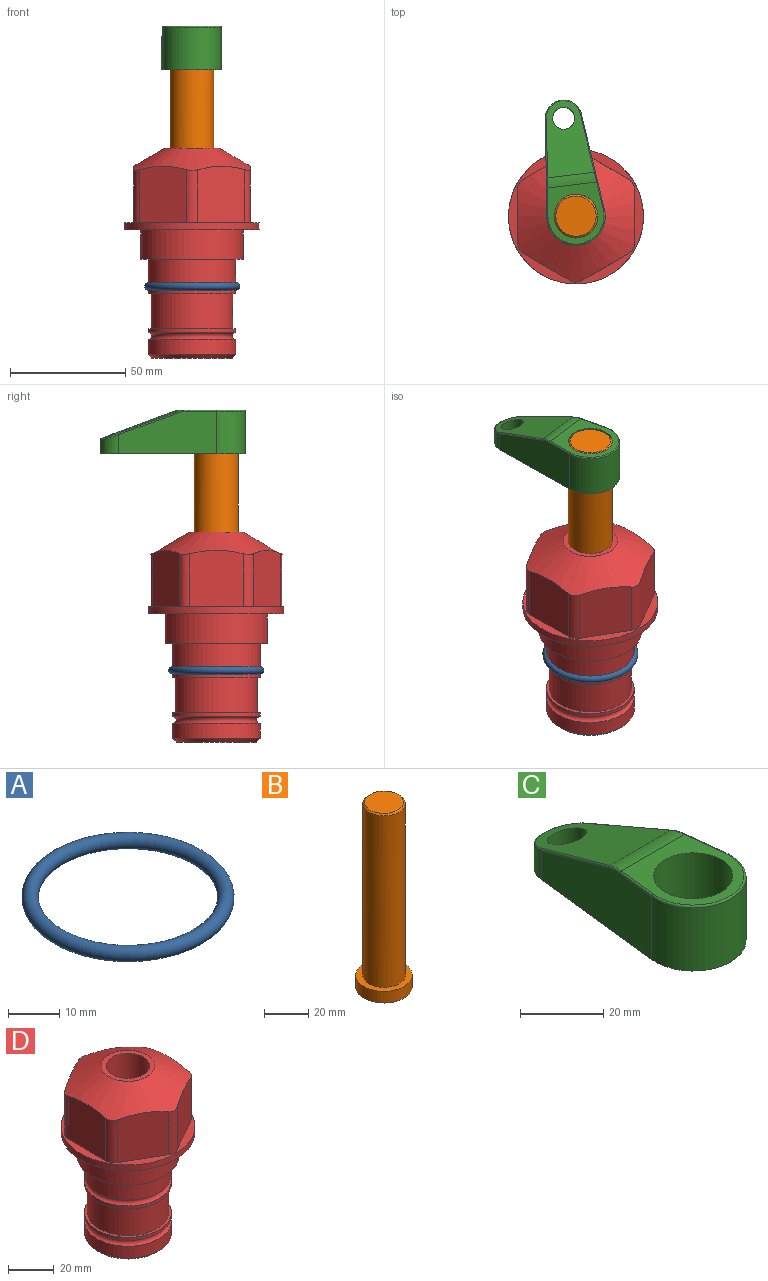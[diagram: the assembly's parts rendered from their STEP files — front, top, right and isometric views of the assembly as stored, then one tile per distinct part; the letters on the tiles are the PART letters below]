
ASSEMBLY  parts=4 mates=2
PART A: 1 faces, bbox 44.7x44.7x3.2 mm
  f0: torus R=19.05mm, axis (0,0,1), area 1193.9mm2
PART B: 6 faces, bbox 25.4x25.4x101.6 mm
  f0: plane 17.46x17.46mm, normal (0,0,1), area 239.5mm2, adj f5
  f1: plane 25.4x25.4mm, normal (0,0,-1), area 506.7mm2, adj f2
  f2: cylinder r=12.7mm len=25.4mm, axis (0,0,1), area 506.7mm2, adj f1,f3
  f3: plane 25.4x25.4mm, normal (0,0,1), area 221.7mm2, adj f2,f4
  f4: cylinder r=9.53mm len=94.46mm, axis (0,0,1), area 5653mm2, adj f3,f5
  f5: cone r=8.73mm half-angle=45deg, axis (0,0,-1), area 64.4mm2, adj f0,f4
PART C: 44 faces, bbox 27.5x64.5x19.1 mm
  f0: plane 2.3x0.95mm, normal (0,0,-1), area 1mm2, adj f25,f30,f34
  f1: plane 63.5x25.4mm, normal (0,0,-1), area 561.7mm2, adj f2,f3,f4,f5,f6,f7,f19,f20
  f2: cylinder r=12.7mm len=25.4mm, axis (0,0,-1), area 792.2mm2, adj f1,f3,f5,f13
  f3: plane 42.33x18.54mm, normal (0.99,0.11,0), area 647mm2, adj f1,f2,f4,f11,f12,f14
  f4: cylinder r=7.94mm len=15.78mm, axis (0,0,-1), area 158.6mm2, adj f1,f3,f5,f16
  f5: plane 42.33x18.54mm, normal (-0.99,0.11,0), area 647mm2, adj f1,f2,f4,f15,f17,f18
  f6: cylinder r=9.53mm len=19.05mm, axis (0,0,-1), area 1140.1mm2, adj f1,f8
  f7: cylinder r=4.76mm len=10.98mm, axis (0,0,-1), area 276.1mm2, adj f1,f9
  f8: plane 25.83x24.38mm, normal (0,0,1), area 262.2mm2, adj f6,f10,f11,f13,f15
  f9: plane 32.49x20.55mm, normal (0,0.34,0.94), area 489.9mm2, adj f7,f10,f14,f16,f18
  f10: cylinder r=12.7mm len=21.49mm, axis (-1,0,0), area 93.2mm2, adj f8,f9,f12,f17
  f11: cylinder r=0.51mm len=12.34mm, axis (0.11,-0.99,0), area 9.9mm2, adj f3,f8,f12,f13
  f12: bspline ~7.62x1.64mm, area 3.5mm2, adj f3,f10,f11,f14
  f13: torus R=12.19mm, axis (0,0,1), area 33.6mm2, adj f2,f8,f11,f15
  f14: cylinder r=0.51mm len=26.01mm, axis (0.1,-0.93,0.34), area 21.6mm2, adj f3,f9,f12,f16
  f15: cylinder r=0.51mm len=12.34mm, axis (0.11,0.99,0), area 9.9mm2, adj f5,f8,f13,f17
  f16: bspline ~15.78x7.05mm, area 15.7mm2, adj f4,f9,f14,f18
  f17: bspline ~7.62x1.64mm, area 3.5mm2, adj f5,f10,f15,f18
  f18: cylinder r=0.51mm len=26.01mm, axis (0.1,0.93,-0.34), area 21.6mm2, adj f5,f9,f16,f17
  f19: plane 21.6x14.29mm, normal (-0.99,-0.11,0), area 242.6mm2, adj f1,f26,f28,f34,f36,f38
  f20: plane 21.6x14.29mm, normal (0.99,-0.11,0), area 242.6mm2, adj f1,f27,f29,f37,f39,f41
  f21: cylinder r=12.7mm len=14.29mm, axis (0,0,-1), area 173.2mm2, adj f1,f26,f27,f30,f31,f33
  f22: cylinder r=7.94mm len=7.63mm, axis (0,0,-1), area 53.8mm2, adj f1,f28,f29,f42
  f23: plane 2.3x0.95mm, normal (0,0,-1), area 1mm2, adj f25,f33,f37
  f24: plane 17.94x12.32mm, normal (0,-0.34,-0.94), area 191.2mm2, adj f25,f38,f41,f42
  f25: cylinder r=9.53mm len=12.93mm, axis (-1,0,0), area 37.5mm2, adj f0,f23,f24,f31,f36,f39
  f26: cylinder r=1.59mm len=14.29mm, axis (0,0,-1), area 49mm2, adj f1,f19,f21,f32
  f27: cylinder r=1.59mm len=14.29mm, axis (0,0,-1), area 49mm2, adj f1,f20,f21,f35
  f28: cylinder r=1.59mm len=7.28mm, axis (0,0,-1), area 22.1mm2, adj f1,f19,f22,f40
  f29: cylinder r=1.59mm len=7.28mm, axis (0,0,-1), area 22.1mm2, adj f1,f20,f22,f43
  f30: torus R=14.29mm, axis (0,0,1), area 5.8mm2, adj f0,f21,f31,f32
  f31: bspline ~11.06x2.73mm, area 20.8mm2, adj f21,f25,f30,f33
  f32: sphere r=1.59mm, area 5.4mm2, adj f26,f30,f34
  f33: torus R=14.29mm, axis (0,0,1), area 5.8mm2, adj f21,f23,f31,f35
  f34: cylinder r=1.59mm len=1.68mm, axis (-0.11,0.99,0), area 2.4mm2, adj f0,f19,f32,f36
  f35: sphere r=1.59mm, area 5.4mm2, adj f27,f33,f37
  f36: bspline ~5.82x2.33mm, area 7.7mm2, adj f19,f25,f34,f38
  f37: cylinder r=1.59mm len=1.68mm, axis (0.11,0.99,0), area 2.4mm2, adj f20,f23,f35,f39
  f38: cylinder r=1.59mm len=18.33mm, axis (0.1,-0.93,0.34), area 46.7mm2, adj f19,f24,f36,f40
  f39: bspline ~5.82x2.33mm, area 7.7mm2, adj f20,f25,f37,f41
  f40: sphere r=1.59mm, area 3.6mm2, adj f28,f38,f42
  f41: cylinder r=1.59mm len=18.33mm, axis (0.1,0.93,-0.34), area 46.7mm2, adj f20,f24,f39,f43
  f42: bspline ~8.31x1.84mm, area 15.3mm2, adj f22,f24,f40,f43
  f43: sphere r=1.59mm, area 3.6mm2, adj f29,f41,f42
PART D: 36 faces, bbox 58.7x58.7x91.2 mm
  f0: cylinder r=17.78mm len=35.56mm, axis (0,0,1), area 1670.8mm2, adj f23,f24,f31
  f1: cylinder r=19.05mm len=38.1mm, axis (0,0,1), area 1191.9mm2, adj f26,f27,f30
  f2: plane 58.66x58.66mm, normal (0,0,-1), area 1150.6mm2, adj f3,f28
  f3: cylinder r=29.33mm len=58.66mm, axis (0,0,-1), area 585.1mm2, adj f2,f4
  f4: plane 58.66x58.66mm, normal (0,0,1), area 475.9mm2, adj f3,f5,f6,f7,f8,f9,f10,f11
  f5: plane 24.5x20.32mm, normal (-0.5,0.87,0), area 562.8mm2, adj f4,f15,f16,f17
  f6: plane 24.5x20.32mm, normal (0.5,0.87,0), area 562.8mm2, adj f4,f14,f15,f17
  f7: plane 24.5x23.48mm, normal (1,0,0), area 562.8mm2, adj f4,f13,f14,f17
  f8: plane 24.5x20.32mm, normal (0.5,-0.87,0), area 562.8mm2, adj f4,f12,f13,f17
  f9: plane 24.5x20.32mm, normal (-0.5,-0.87,0), area 562.8mm2, adj f4,f11,f12,f17
  f10: plane 24.5x23.48mm, normal (-1,0,0), area 562.8mm2, adj f4,f11,f16,f17
  f11: cylinder r=5.08mm len=23.01mm, axis (0,0,-1), area 121.2mm2, adj f4,f9,f10,f17
  f12: cylinder r=5.08mm len=23.01mm, axis (0,0,-1), area 121.2mm2, adj f4,f8,f9,f17
  f13: cylinder r=5.08mm len=23.01mm, axis (0,0,-1), area 121.2mm2, adj f4,f7,f8,f17
  f14: cylinder r=5.08mm len=23.01mm, axis (0,0,-1), area 121.2mm2, adj f4,f6,f7,f17
  f15: cylinder r=5.08mm len=23.01mm, axis (0,0,-1), area 121.2mm2, adj f4,f5,f6,f17
  f16: cylinder r=5.08mm len=23.01mm, axis (0,0,-1), area 121.2mm2, adj f4,f5,f10,f17
  f17: cone r=11.73mm half-angle=60deg, axis (0,0,-1), area 2071.8mm2, adj f5,f6,f7,f8,f9,f10,f11,f12
  f18: plane 23.46x23.46mm, normal (0,0,1), area 147.4mm2, adj f17,f35
  f19: plane 34.93x34.93mm, normal (0,0,-1), area 958mm2, adj f29
  f20: cylinder r=19.05mm len=38.1mm, axis (0,0,1), area 760.1mm2, adj f21,f29
  f21: torus R=19.05mm, axis (0,0,1), area 565.3mm2, adj f20,f22
  f22: cylinder r=19.05mm len=38.1mm, axis (0,0,1), area 190mm2, adj f21,f23
  f23: plane 38.1x38.1mm, normal (0,0,1), area 146.9mm2, adj f0,f22
  f24: plane 38.1x38.1mm, normal (0,0,-1), area 146.9mm2, adj f0,f25
  f25: cylinder r=19.05mm len=38.1mm, axis (0,0,1), area 190mm2, adj f24,f26
  f26: torus R=19.05mm, axis (0,0,1), area 565.3mm2, adj f1,f25
  f27: plane 44.45x44.45mm, normal (0,0,-1), area 411.7mm2, adj f1,f28
  f28: cylinder r=22.23mm len=44.45mm, axis (0,0,1), area 1773.5mm2, adj f2,f27
  f29: cone r=19.05mm half-angle=45deg, axis (0,0,1), area 257.5mm2, adj f19,f20
  f30: cylinder r=3.17mm len=6.75mm, axis (-1,0,0), area 128mm2, adj f1,f33
  f31: cylinder r=3.17mm len=6.35mm, axis (-1,0,0), area 102.5mm2, adj f0,f33
  f32: plane 25.4x25.4mm, normal (0,0,1), area 506.7mm2, adj f33
  f33: cylinder r=12.7mm len=66.42mm, axis (0,0,-1), area 5236.2mm2, adj f30,f31,f32,f34
  f34: cone r=9.53mm half-angle=30deg, axis (0,0,-1), area 443.4mm2, adj f33,f35
  f35: cylinder r=9.53mm len=19.05mm, axis (0,0,-1), area 849mm2, adj f18,f34
PLACE A at identity
PLACE B rot(axis=(0,0,1),7.2deg) t=(0,0,14.96)mm
PLACE C rot(axis=(0,0,1),7.2deg) t=(0,0,69.57)mm
PLACE D at identity fixed
MATE fastened C.f2 <-> B.f2  axis (0,0,-1) through (0,0,88.62)mm
MATE cylindrical B.f2 <-> D.f0  axis (0,0,1) through (0,0,40.6)mm
